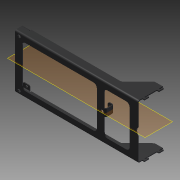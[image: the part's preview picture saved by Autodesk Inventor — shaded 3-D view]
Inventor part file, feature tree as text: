
AUTODESK INVENTOR PART (.ipt)
format: ipt  version: 2015 (Build 190159000, 159)  size: 468,992 bytes
history: native  units: mm
features: extrude x9, fillet x6, mirror x2, hole x2, projected_geometry x2, shell x1, other x1
ambient origin geometry x8: Origin, YZ Plane, XZ Plane, XY Plane, X Axis, Y Axis, Z Axis, Center Point
bodies: Solid1 (feature_tree)
feature tree (23):
  extrude  "Extrusión1"  Depth=60.0mm
  fillet  "Empalme7"  Radius=295.0mm
  shell  "Vaciado2"  Thickness=20.0mm
  extrude  "Extrusión10"  Depth=20.0mm
  fillet  "Empalme8"  Radius=130.0mm
  extrude  "Extrusión11"  TaperAngle=45.0deg  [1 undecoded]
  extrude  "Extrusión12"  Depth=4.0mm
  mirror  "Simetría1"
  hole  "Agujero6"  [1 undecoded]
  fillet  "Empalme9"  Radius=15.0mm
  fillet  "Empalme11"  Radius=15.0mm
  extrude  "Extrusión13"  Depth=17.0mm
  extrude  "Extrusión14"  Depth=20.0mm
  extrude  "Extrusión15"  Depth=10.0mm TaperAngle=0.0deg
  hole  "Agujero7"  [1 undecoded]
  fillet  "Redondeo de esquina1"  Radius=3.0mm
  extrude  "Extrusión16"  Depth=6.0mm
  fillet  "Redondeo de esquina2"  Radius=10.0mm
  mirror  "Simetría2"
  extrude  "Extrusión17"  Depth=52.0mm TaperAngle=0.0deg
  projected_geometry  "Contorno proyectado4"
  projected_geometry  "Contorno proyectado5"
  other  "Definición1"
note: 3 required parameter values undecoded (feature->parameter linkage not recoverable at this tier; creation-order binding heuristic only, values carry confidence <= 0.55)
